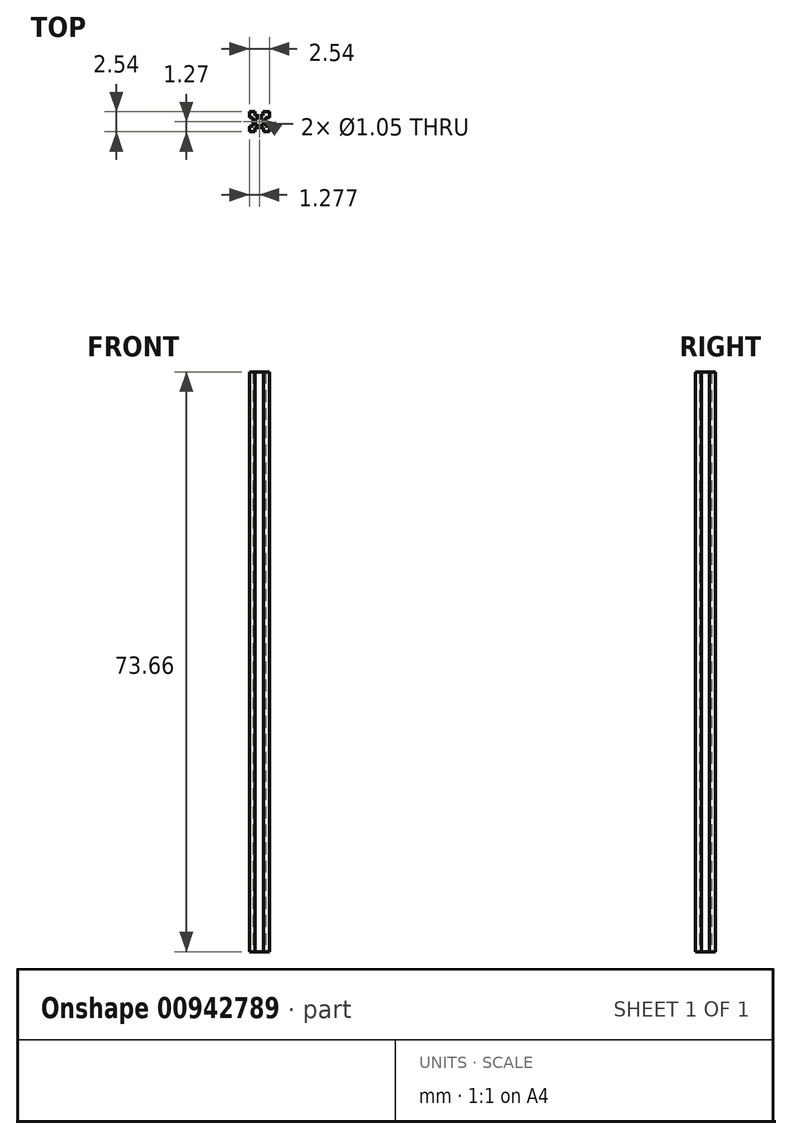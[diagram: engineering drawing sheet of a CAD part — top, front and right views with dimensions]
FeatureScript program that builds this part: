
annotation { "Feature Type Name" : "Feature", "Feature Type Description" : "" }
export const myFeature = defineFeature(function(context is Context, id is Id, definition is map)
    precondition{}
    {
        {
            var Q0;
            Q0=qCreatedBy(makeId("Top.planeOp"),FACE);
            var sketch = newSketch(context, id + "F0", { "sketchPlane" : qUnion([Q0])});
            skLineSegment(sketch, "E0.bottom", {"start": v(0, 0) * mm, "end": v(2.54, 0) * mm});
            skLineSegment(sketch, "E0.top", {"start": v(0, 2.54) * mm, "end": v(2.54, 2.54) * mm});
            skLineSegment(sketch, "E0.left", {"start": v(0, 0) * mm, "end": v(0, 2.54) * mm});
            skLineSegment(sketch, "E0.right", {"start": v(2.54, 0) * mm, "end": v(2.54, 2.54) * mm});
            skLineSegment(sketch, "E1", {"start": v(0, 1.27) * mm, "end": v(1.28, 1.27) * mm});
            skCircle(sketch, "E2", {"center": v(1.28, 1.27) * mm, "radius": 0.52 * mm});
            skLineSegment(sketch, "E3.bottom", {"start": v(0.7, 2.54) * mm, "end": v(1.78, 2.54) * mm});
            skLineSegment(sketch, "E3.top", {"start": v(0.7, 2.03) * mm, "end": v(1.78, 2.03) * mm});
            skLineSegment(sketch, "E3.left", {"start": v(0.7, 2.54) * mm, "end": v(0.7, 2.03) * mm});
            skLineSegment(sketch, "E3.right", {"start": v(1.78, 2.54) * mm, "end": v(1.78, 2.03) * mm});
            skLineSegment(sketch, "E4.bottom", {"start": v(1.83, 0) * mm, "end": v(0.76, 0) * mm});
            skLineSegment(sketch, "E4.top", {"start": v(1.83, 0.5) * mm, "end": v(0.76, 0.5) * mm});
            skLineSegment(sketch, "E4.left", {"start": v(1.83, 0) * mm, "end": v(1.83, 0.5) * mm});
            skLineSegment(sketch, "E4.right", {"start": v(0.76, 0) * mm, "end": v(0.76, 0.5) * mm});
            skLineSegment(sketch, "E5.bottom", {"start": v(2.54, 1.78) * mm, "end": v(2.04, 1.78) * mm});
            skLineSegment(sketch, "E5.top", {"start": v(2.54, 0.75) * mm, "end": v(2.04, 0.75) * mm});
            skLineSegment(sketch, "E5.left", {"start": v(2.54, 1.78) * mm, "end": v(2.54, 0.75) * mm});
            skLineSegment(sketch, "E5.right", {"start": v(2.04, 1.78) * mm, "end": v(2.04, 0.75) * mm});
            skLineSegment(sketch, "E6.bottom", {"start": v(0, 0.75) * mm, "end": v(0.5, 0.75) * mm});
            skLineSegment(sketch, "E6.top", {"start": v(0, 1.78) * mm, "end": v(0.5, 1.78) * mm});
            skLineSegment(sketch, "E6.left", {"start": v(0, 0.75) * mm, "end": v(0, 1.78) * mm});
            skLineSegment(sketch, "E6.right", {"start": v(0.5, 0.75) * mm, "end": v(0.5, 1.78) * mm});
            skSolve(sketch);
        }
        {
            var Q0;
            Q0=makeQuery(id+"F0.imprint","IMPRINT",FACE,{"disambiguationData":[TD([[makeQuery(id+"F0.imprint","IMPRINT",EDGE,{"derivedFrom":sQuery(id+"F0.wireOp",EDGE,"E2")}),-1.0]])]});
            extrude(context, id + "F1", {"entities" : qUnion([Q0]), "depth" : 73.66 * mm, "offsetDistance" : 25.4 * mm});
        }
    });
